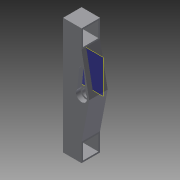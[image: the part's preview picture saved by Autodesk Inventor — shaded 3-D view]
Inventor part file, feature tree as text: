
AUTODESK INVENTOR PART (.ipt)
format: ipt  version: 2015 (Build 190159000, 159)  size: 123,904 bytes
history: native  units: mm
features: other x4, sketch x3, extrude x3, mirror x1, hole x1
ambient origin geometry x8: Origin, YZ Plane, XZ Plane, XY Plane, X Axis, Y Axis, Z Axis, Center Point
bodies: Body1 (feature_tree), Body2 (feature_tree), Body3 (feature_tree)
feature tree (12):
  other  "작업 평면1"
  sketch  "스케치1"
  other  "작업 평면2"
  extrude  "돌출1"  Depth=9.0mm TaperAngle=0.0deg
  extrude  "돌출3"  Depth=26.0mm
  mirror  "대칭2"
  extrude  "돌출4"  TaperAngle=90.0deg  [1 undecoded]
  hole  "구멍1"  [1 undecoded]
  other  "두껍게 하기1"
  sketch  "스케치3"
  sketch  "스케치5"
  other  "솔리드1"
note: 2 required parameter values undecoded (feature->parameter linkage not recoverable at this tier; creation-order binding heuristic only, values carry confidence <= 0.55)
